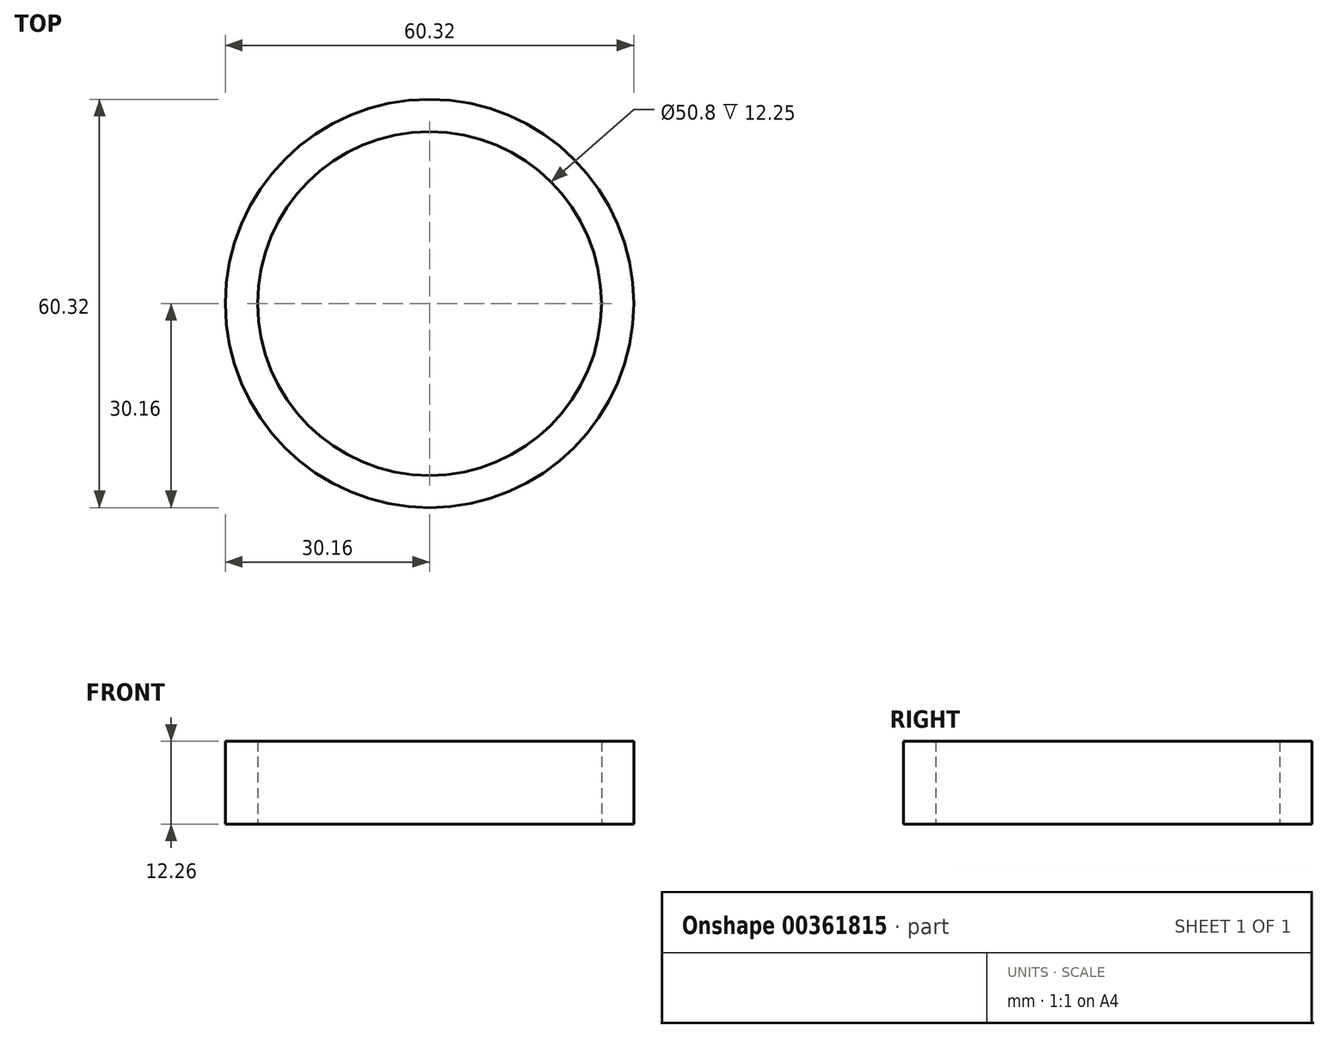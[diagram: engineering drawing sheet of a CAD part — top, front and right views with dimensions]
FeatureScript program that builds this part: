
annotation { "Feature Type Name" : "Feature", "Feature Type Description" : "" }
export const myFeature = defineFeature(function(context is Context, id is Id, definition is map)
    precondition{}
    {
        {
            var Q0;
            Q0=qCreatedBy(makeId("Top.planeOp"),FACE);
            var sketch = newSketch(context, id + "F0", { "sketchPlane" : qUnion([Q0])});
            skCircle(sketch, "E0", {"center": v(0, 0) * mm, "radius": 25.4 * mm});
            skCircle(sketch, "E1", {"center": v(0, 0) * mm, "radius": 30.16 * mm});
            skSolve(sketch);
        }
        {
            var Q0;
            Q0=makeQuery(id+"F0.imprint","IMPRINT",FACE,{"disambiguationData":[TD([[makeQuery(id+"F0.imprint","IMPRINT",EDGE,{"derivedFrom":sQuery(id+"F0.wireOp",EDGE,"E0")}),-1.0]])]});
            extrude(context, id + "F1", {"entities" : qUnion([Q0]), "depth" : (6 + (1 / 8)) * mm, "hasSecondDirection" : true, "secondDirectionOppositeDirection" : true, "secondDirectionDepth" : (6 + (1 / 8)) * mm});
        }
    });
